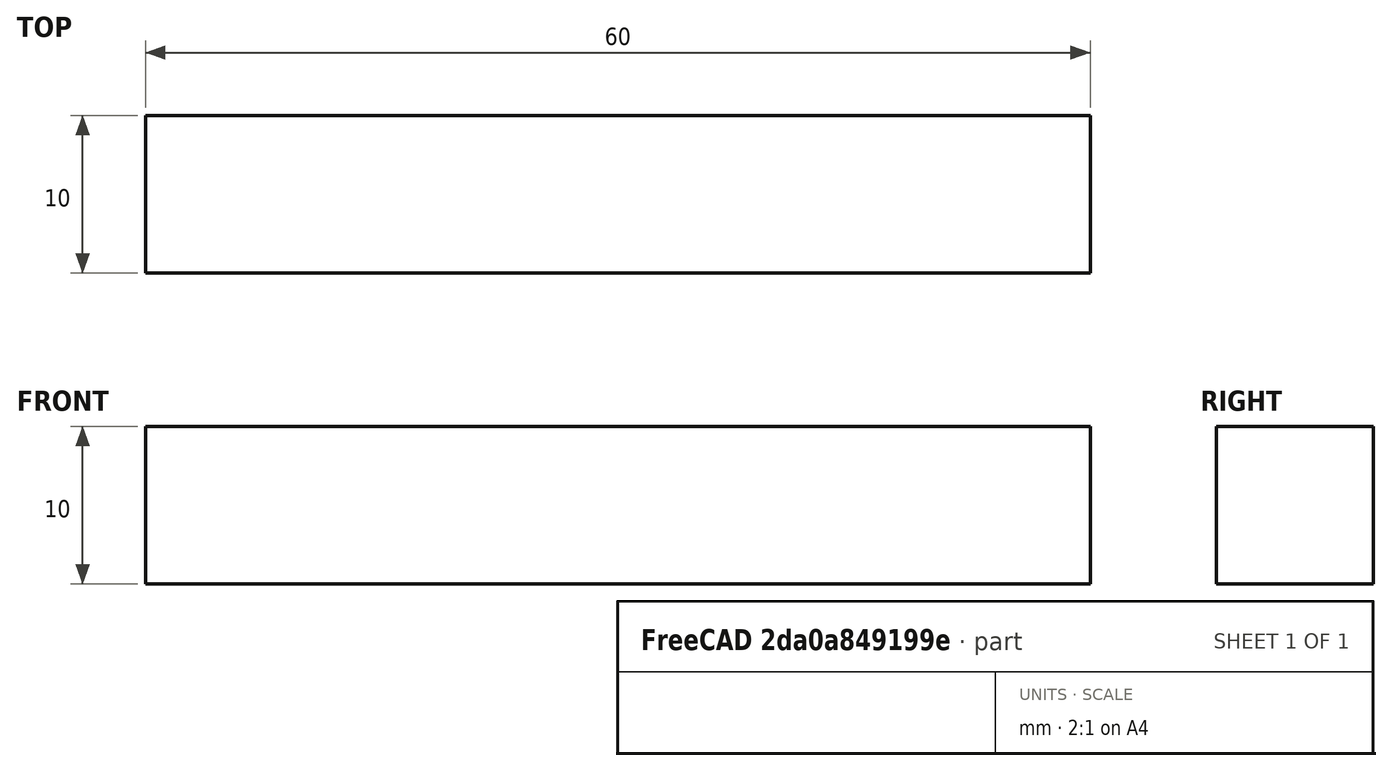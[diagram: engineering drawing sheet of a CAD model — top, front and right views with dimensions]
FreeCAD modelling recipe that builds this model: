
FCSTD DOCUMENT  (FreeCAD 0.18R4 (GitTag))
Label: pc_fan_bracket
License: All rights reserved
LicenseURL: http://en.wikipedia.org/wiki/All_rights_reserved
objects: Sketcher::SketchObject×1, PartDesign::Pad×1, PartDesign::Body×1
note: 4 computed .brp shape members not serialized (recipe doc carries the construction recipe); baked Part::Feature solids carry a one-line shape summary decoded from their .brp

FEATURE [Sketcher::SketchObject] Sketch
  MapMode = 5
  Placement = pos=(0,0,0) rot=(0.57735,0.57735,0.57735;2.0944rad)
  Support = -> [YZ_Plane]
  sketch-geometry (4):
    g0: LineSegment StartX=0 StartY=0 StartZ=0 EndX=-10 EndY=0 EndZ=0
    g1: LineSegment StartX=-10 StartY=0 StartZ=0 EndX=-10 EndY=10 EndZ=0
    g2: LineSegment StartX=-10 StartY=10 StartZ=0 EndX=0 EndY=10 EndZ=0
    g3: LineSegment StartX=0 StartY=10 StartZ=0 EndX=0 EndY=0 EndZ=0
  constraints (11):
    c: Coincident(g0,g1)
    c: Coincident(g1,g2)
    c: Coincident(g2,g3)
    c: Coincident(g3,g0)
    c: Horizontal(g0)
    c: Horizontal(g2)
    c: Vertical(g1)
    c: Vertical(g3)
    c: Coincident(g0,g-1)
    c: DistanceX(g0,g0) = 10
    c: DistanceY(g3,g3) = 10
FEATURE [PartDesign::Pad] Pad
  Length = 60
  Length2 = 100
  Placement = pos=(0,0,0) rot=(0.57735,0.57735,0.57735;2.0944rad)
  Profile = -> Sketch
  Type = 0
FEATURE [PartDesign::Body] Body
  Group = -> [Sketch,Pad]
  Origin = -> Origin
  Tip = -> Pad
